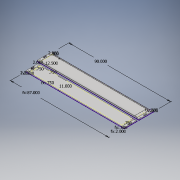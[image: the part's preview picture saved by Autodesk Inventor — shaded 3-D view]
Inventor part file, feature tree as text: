
AUTODESK INVENTOR PART (.ipt)
format: ipt  version: 2018 (Build 220112000, 112)  size: 311,808 bytes
history: native  units: in
note: dims shown in document units (in); Inventor stores cm internally (conversion verified against a paired STEP export)
features: projected_geometry x6, extrude x5, other x4, hole x1
ambient origin geometry x8: Origin, YZ Plane, XZ Plane, XY Plane, X Axis, Y Axis, Z Axis, Center Point
bodies: Solid1 (feature_tree)
feature tree (16):
  other  "Base Sketch"
  extrude  "Lower Level"  Depth=0.75in TaperAngle=0.0deg
  extrude  "Base"  Depth=0.125in TaperAngle=0.0deg
  other  "Tracks Sketch"
  extrude  "Pocket side"  Depth=0.5in TaperAngle=0.0deg
  extrude  "Tracks"  Depth=2.0in
  other  "Handle Sketch"
  other  "Origin Sketch"
  extrude  "Handles"  Depth=2.0in
  hole  "Hole1"  [1 undecoded]
  projected_geometry  "Projected Loop1"
  projected_geometry  "Projected Loop2"
  projected_geometry  "Projected Loop3"
  projected_geometry  "Projected Loop4"
  projected_geometry  "Projected Loop5"
  projected_geometry  "Projected Loop6"
note: 1 required parameter value undecoded (feature->parameter linkage not recoverable at this tier; creation-order binding heuristic only, values carry confidence <= 0.55)
